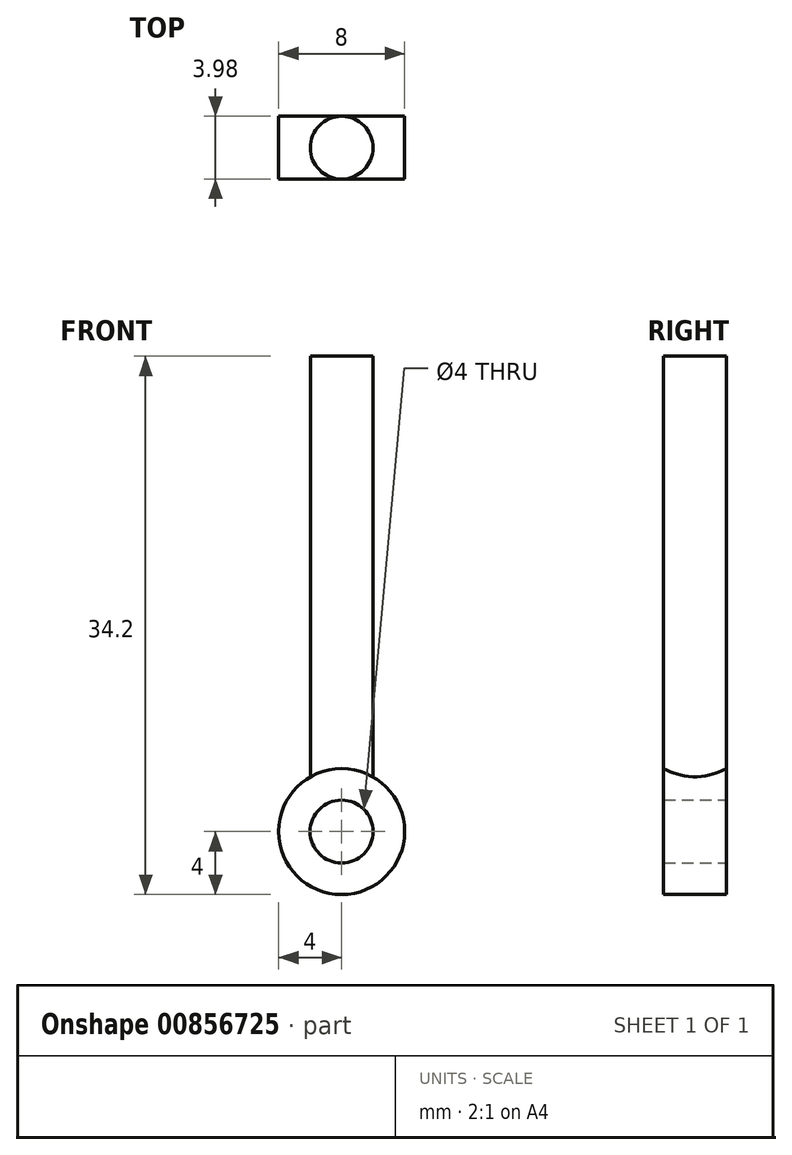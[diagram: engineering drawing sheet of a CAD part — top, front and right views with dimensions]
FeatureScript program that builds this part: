
annotation { "Feature Type Name" : "Feature", "Feature Type Description" : "" }
export const myFeature = defineFeature(function(context is Context, id is Id, definition is map)
    precondition{}
    {
        {
            var Q0;
            Q0=qCreatedBy(makeId("Front.planeOp"),FACE);
            var sketch = newSketch(context, id + "F0", { "sketchPlane" : qUnion([Q0])});
            skCircle(sketch, "E0", {"center": v(0, 0) * mm, "radius": 2 * mm});
            skCircle(sketch, "E1", {"center": v(0, 0) * mm, "radius": 4 * mm});
            skLineSegment(sketch, "E2.top", {"start": v(-2.58, 82.67) * mm, "end": v(2.75, 82.67) * mm});
            skSolve(sketch);
        }
        {
            var Q0;
            Q0=qSketchRegion(id+"F0",true);
            extrude(context, id + "F1", {"entities" : qUnion([Q0]), "endBound" : BoundingType.SYMMETRIC, "depth" : 3.8 * mm, "offsetDistance" : 25 * mm});
        }
        {
            var Q0;
            Q0 = qSketchRegion(id + "F0", true);
            extrude(context, id + "F2", {"entities" : qUnion([Q0]), "operationType" : NewBodyOperationType.ADD, "endBound" : BoundingType.SYMMETRIC, "depth" : 3.98 * mm, "offsetDistance" : 25 * mm});
        }
        {
            var Q0;
            Q0=qCreatedBy(makeId("Top.planeOp"),FACE);
            cPlane(context, id + "F3", {"entities" : qUnion([Q0]), "cplaneType" : CPlaneType.OFFSET, "offset" : 2.2 * mm, "width" : 150 * mm, "height" : 150 * mm});
        }
        {
            var Q0;
            Q0=qCreatedBy(id+"F3.planeOp",FACE);
            var sketch = newSketch(context, id + "F4", { "sketchPlane" : qUnion([Q0])});
            skCircle(sketch, "E3", {"center": v(0, 0) * mm, "radius": 1.99 * mm});
            skSolve(sketch);
        }
        {
            var Q0;
            Q0 = qSketchRegion(id + "F4", true);
            extrude(context, id + "F5", {"entities" : qUnion([Q0]), "operationType" : NewBodyOperationType.ADD, "depth" : 28 * mm, "offsetDistance" : 25 * mm});
        }
    });
